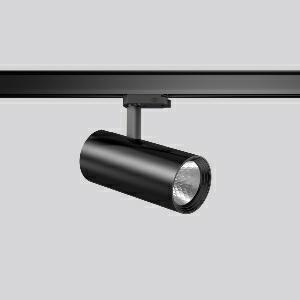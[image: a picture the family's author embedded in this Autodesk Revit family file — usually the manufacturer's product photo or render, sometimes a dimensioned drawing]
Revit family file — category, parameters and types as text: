
# Revit family: deecos_s_mini_742195_003_1_1ab3
name_source: partatom
category: Lighting Fixtures
units: mm (PartAtom-declared; Revit-internal decimal feet)

## family parameters
Cut with Voids When Loaded = No
Host = Face
Light Source = No
Part Type = Normal
Room Calculation Point = No
Round Connector Dimension = Use Diameter
Shared = No

## types (1)
- DEECOS S mini (1 x LED Modul 940, 2700 lm, 4000)
    Apparent Load = 20 VA
    Approval mark = CE
    CIE Flux Codes = 100 100 100 100 100
    Color Rendering = 92
    Color Temperature = 4000
    Default Elevation = 1800 mm
    Description = Series: DEECOS S mini
LED surface-mounted projector in modern design with no visible cooling ribs. Housing: die-cast aluminium, powder-coated. Rotation range: 356°. Swivel range: 90°. Black plastic ring and recessed LED to prevent glare from the side. Optical assembly with reflector made of MIRO-Silver with 98% total light reflection for outstanding efficiency - can be changed without tools. Best colour rendering index Ra>90. With multi adaptor for 3-circuit tracks 230 V. Suitable for Track on ceiling, Wall track. High quality converter without flickering and stroboscopic effect. The following accessories can be mounted without use of tools: interchangeable lenses, decorative glasses, honeycomb louvre, clear and frosted diffusers, white interchangeable plastic ring. 
Colour: deep black, matt (RAL 9005)
Diameter: 87 mm
Height: 214 mm
Lamp: LED
Socket: without socket
Colour temperature: 4000K
Colour rendering index (CRI): 92
System power: 20 W
Rated luminous flux: 2700 lm
Luminous efficiency: 135 lm/W
Control gear: Regulated power supply
Protection class: I
Type of protection: IP 20
    Height = 214 mm
    Lamp = 1 x LED Modul 940
    Lamp Light Flux = 2700 lm
    Lamp count = 1
    Length = 87 mm
    Lifetime = 50000 h
    Luminous efficacy = 135 lm/W
    Manufacturer = RZB
    ModVariant = No
    Model = 742195.003.1
    Mounting Place = Ceiling
    Mounting Type = Rail mounted
    Number of Poles = 1
    OnlyDefault = Yes
    Power Factor = 1
    Product Name = DEECOS S mini
    Product group = Track mounted projectors
    ProductGroupID = 301
    Protection Class = Protection class I
    Protection Degree = IP 20
    RLX_Detail_Level = 1
    RLX_Emergency_Light_Flux = 0 lm
    RLX_Emergency_Type = 0
    RLX_Emergency_Type_DB = No
    RlxData = <blob elided: 38921 chars, md5=9eeb0f07>
    Socket = socket
    Standby Power = 0 W
    System Light Flux = 2700 lm
    System Power = 20 W
    Type Comments = Product without accessories
    Type Image = 741926.003.jpg
    URL = http://relux.com
    VarID = ---
    Voltage = 230 V
    Voltage Range = 220-240 V
    Weight = 0.00 kg
    Width = 0 mm  [stored 0 ft]

note: [stored X ft] marks values corroborated as IEEE doubles in the binary element streams (Revit-internal decimal feet)

## geometry (parser evidence)
native form markers: Blend x4, Sweep x10
no freeform markers — native parametric forms only
